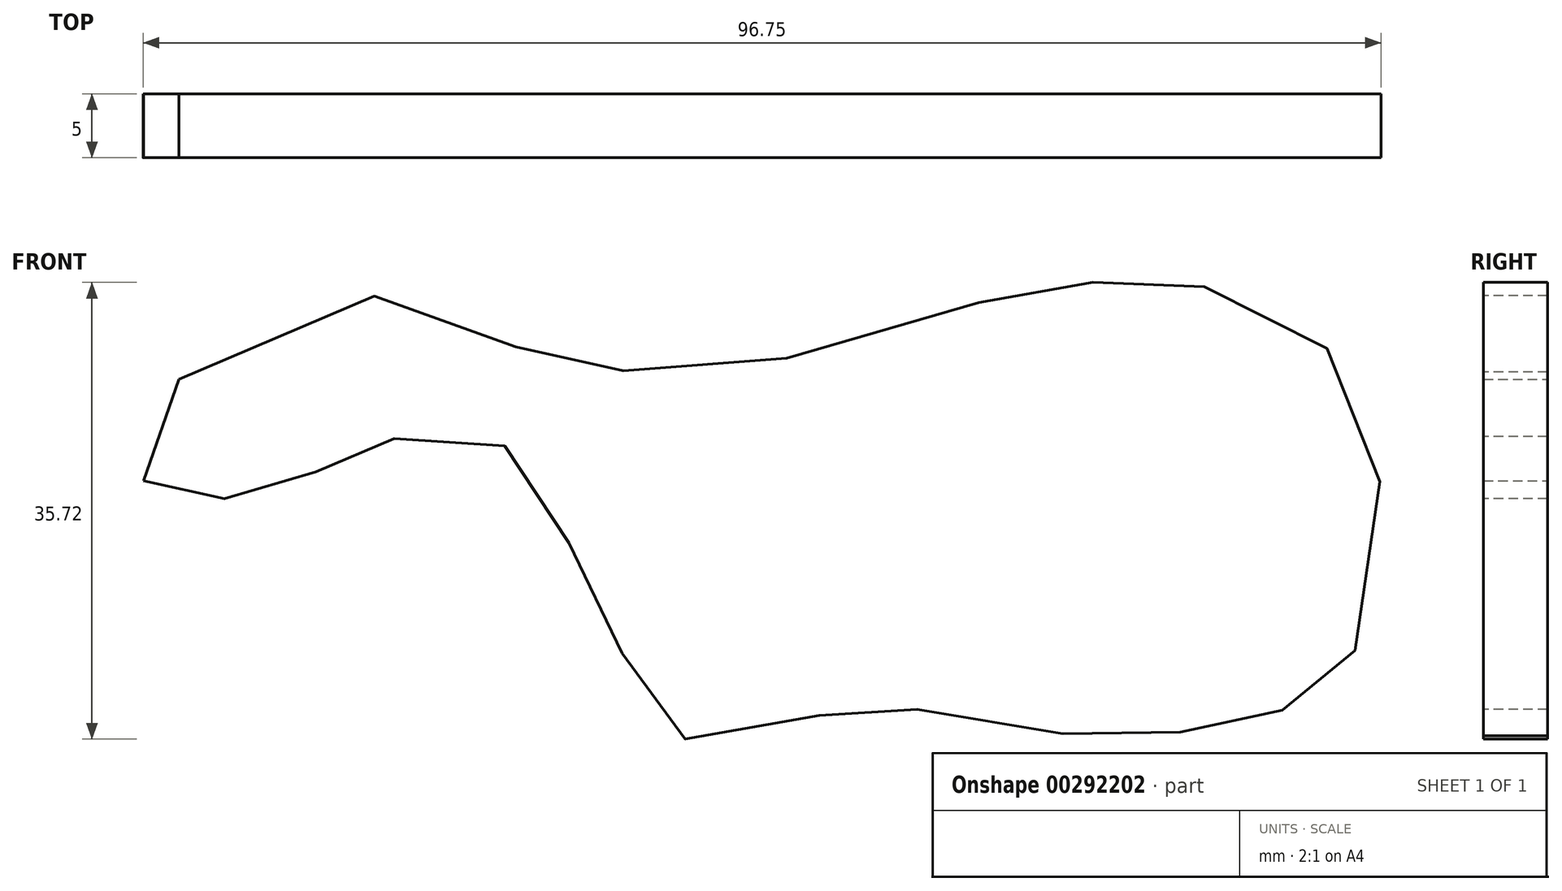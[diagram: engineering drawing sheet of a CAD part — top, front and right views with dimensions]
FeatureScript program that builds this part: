
annotation { "Feature Type Name" : "Feature", "Feature Type Description" : "" }
export const myFeature = defineFeature(function(context is Context, id is Id, definition is map)
    precondition{}
    {
        {
            var Q0;
            Q0=qCreatedBy(makeId("Front.planeOp"),FACE);
            var sketch = newSketch(context, id + "F0", { "sketchPlane" : qUnion([Q0])});
            skFitSpline(sketch, "E0", {"points": [v(-51.31, 11.59) * mm, v(-34.27, 18.13) * mm, v(-25.36, 14.36) * mm, v(-22.19, 12.98) * mm, v(-14.46, 12.18) * mm, v(-2.38, 13.57) * mm, v(12.88, 18.13) * mm, v(17.43, 19.12) * mm, v(24.17, 19.12) * mm, v(28.33, 18.92) * mm, v(35.86, 16.34) * mm, v(41, 9.6) * mm, v(42.6, 0) * mm, v(39.82, -11.2) * mm, v(37.44, -13.17) * mm, v(33.68, -14.76) * mm, v(30.11, -15.75) * mm, v(22.78, -16.15) * mm, v(18.03, -16.15) * mm, v(8.92, -14.36) * mm, v(2.38, -14.36) * mm, v(0, -14.56) * mm, v(-9.11, -15.95) * mm, v(-12.68, -16.34) * mm, v(-15.65, -11.99) * mm, v(-18.62, -5.65) * mm, v(-21.4, 0) * mm, v(-24.76, 5.84) * mm, v(-27.93, 6.64) * mm, v(-34.08, 7.03) * mm, v(-37.05, 5.84) * mm, v(-39.62, 4.85) * mm, v(-43.58, 2.87) * mm, v(-46.95, 2.28) * mm, v(-52.3, 2.67) * mm, v(-54.08, 3.47) * mm, v(-54.08, 3.67) * mm], "startDerivative": vector(365.78, 210.93) * mm, "endDerivative": vector(11.77, 36.66) * mm});
            skFitSpline(sketch, "E1", {"points": [v(-54.08, 3.67) * mm, v(-51.31, 11.59) * mm], "startDerivative": vector(2.77, 7.92) * mm, "endDerivative": vector(2.77, 7.92) * mm});
            skSolve(sketch);
        }
        {
            var Q0;
            Q0 = qSketchRegion(id + "F0", true);
            extrude(context, id + "F1", {"entities" : qUnion([Q0]), "depth" : 5 * mm});
        }
    });
